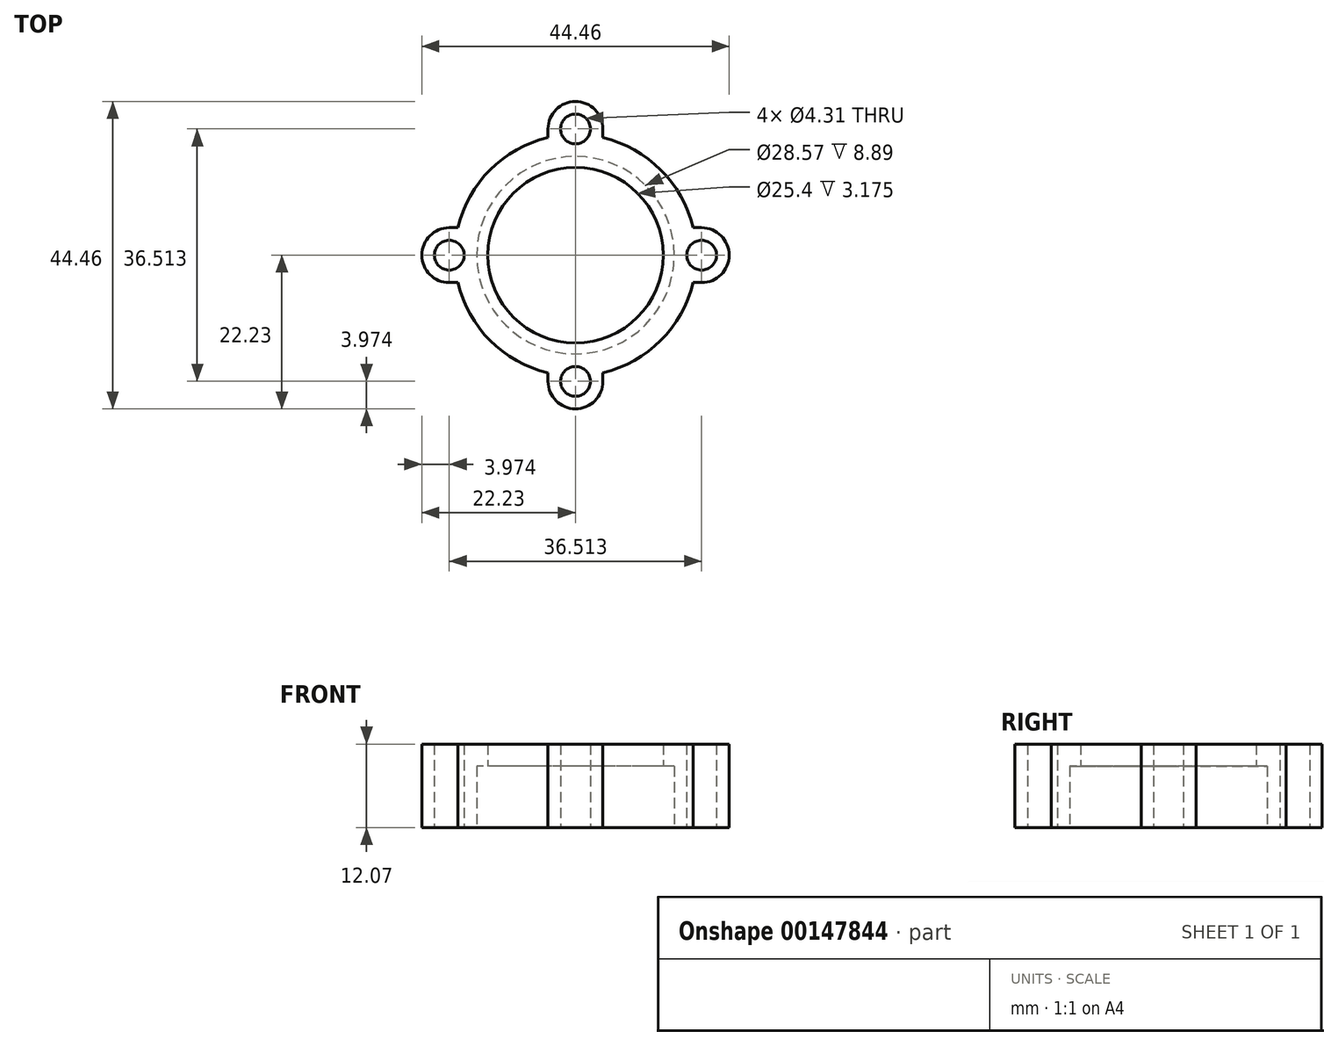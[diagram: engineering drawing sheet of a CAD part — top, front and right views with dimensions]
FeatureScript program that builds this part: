
annotation { "Feature Type Name" : "Feature", "Feature Type Description" : "" }
export const myFeature = defineFeature(function(context is Context, id is Id, definition is map)
    precondition{}
    {
        {
            var Q0;
            Q0=qCreatedBy(makeId("Top.planeOp"),FACE);
            var sketch = newSketch(context, id + "F0", { "sketchPlane" : qUnion([Q0])});
            skCircle(sketch, "E0", {"center": v(0, 0) * mm, "radius": 14.29 * mm});
            skLineSegment(sketch, "E1", {"start": v(-18.26, 0) * mm, "end": v(18.26, 0) * mm, "construction": true});
            skLineSegment(sketch, "E2", {"start": v(0, 18.26) * mm, "end": v(0, -18.26) * mm, "construction": true});
            skLineSegment(sketch, "E3.bottom", {"start": v(-3.97, 18.26) * mm, "end": v(3.97, 18.26) * mm, "construction": true});
            skLineSegment(sketch, "E3.left", {"start": v(3.97, 18.26) * mm, "end": v(3.97, 17) * mm});
            skLineSegment(sketch, "E3.right", {"start": v(-3.97, 18.26) * mm, "end": v(-3.97, 17) * mm});
            skLineSegment(sketch, "E4.bottom", {"start": v(18.26, -3.97) * mm, "end": v(17, -3.97) * mm});
            skLineSegment(sketch, "E4.top", {"start": v(18.26, 3.97) * mm, "end": v(17, 3.97) * mm});
            skLineSegment(sketch, "E4.left", {"start": v(18.26, -3.97) * mm, "end": v(18.26, 3.97) * mm, "construction": true});
            skLineSegment(sketch, "E5.bottom", {"start": v(-3.97, -18.26) * mm, "end": v(3.97, -18.26) * mm, "construction": true});
            skLineSegment(sketch, "E5.left", {"start": v(-3.97, -18.26) * mm, "end": v(-3.97, -17) * mm});
            skLineSegment(sketch, "E5.right", {"start": v(3.97, -18.26) * mm, "end": v(3.97, -17) * mm});
            skLineSegment(sketch, "E6.bottom", {"start": v(-18.26, 3.97) * mm, "end": v(-17, 3.97) * mm});
            skLineSegment(sketch, "E6.top", {"start": v(-18.26, -3.97) * mm, "end": v(-17, -3.97) * mm});
            skLineSegment(sketch, "E6.left", {"start": v(-18.26, 3.97) * mm, "end": v(-18.26, -3.97) * mm, "construction": true});
            skArc(sketch, "E7", {"start": v(17, 3.97) * mm, "mid": v(12.35, 12.35) * mm, "end": v(3.97, 17) * mm});
            skArc(sketch, "E8", {"start": v(-3.97, 17) * mm, "mid": v(-12.35, 12.35) * mm, "end": v(-17, 3.97) * mm});
            skArc(sketch, "E9", {"start": v(-17, -3.97) * mm, "mid": v(-12.35, -12.35) * mm, "end": v(-3.97, -17) * mm});
            skArc(sketch, "E10", {"start": v(3.97, -17) * mm, "mid": v(12.35, -12.35) * mm, "end": v(17, -3.97) * mm});
            skArc(sketch, "E11", {"start": v(3.97, 18.26) * mm, "mid": v(0, 22.22) * mm, "end": v(-3.97, 18.26) * mm});
            skArc(sketch, "E12", {"start": v(18.26, -3.97) * mm, "mid": v(22.22, 0) * mm, "end": v(18.26, 3.97) * mm});
            skArc(sketch, "E13", {"start": v(-3.97, -18.26) * mm, "mid": v(0, -22.22) * mm, "end": v(3.97, -18.26) * mm});
            skArc(sketch, "E14", {"start": v(-18.26, 3.97) * mm, "mid": v(-22.22, 0) * mm, "end": v(-18.26, -3.97) * mm});
            skCircle(sketch, "E15", {"center": v(0, 18.26) * mm, "radius": 2.15 * mm});
            skCircle(sketch, "E16", {"center": v(18.26, 0) * mm, "radius": 2.15 * mm});
            skCircle(sketch, "E17", {"center": v(0, -18.26) * mm, "radius": 2.15 * mm});
            skCircle(sketch, "E18", {"center": v(-18.26, 0) * mm, "radius": 2.15 * mm});
            skArc(sketch, "E19", {"start": v(-3.97, 18.26) * mm, "mid": v(0, 14.29) * mm, "end": v(3.97, 18.26) * mm, "construction": true});
            skSolve(sketch);
        }
        {
            var Q0;
            Q0=qSketchRegion(id+"F0",true);
            extrude(context, id + "F1", {"entities" : qUnion([Q0]), "depth" : 8.9 * mm});
        }
        {
            var Q0;
            Q0=makeQuery(id+"F1.opExtrude","CAP_FACE",FACE,{"disambiguationData":[OSD([sQuery(id+"F0.wireOp",EDGE,"E0"),sQuery(id+"F0.wireOp",EDGE,"E3.left"),sQuery(id+"F0.wireOp",EDGE,"E3.right"),sQuery(id+"F0.wireOp",EDGE,"E4.bottom"),sQuery(id+"F0.wireOp",EDGE,"E4.top"),sQuery(id+"F0.wireOp",EDGE,"E5.left"),sQuery(id+"F0.wireOp",EDGE,"E5.right"),sQuery(id+"F0.wireOp",EDGE,"E6.bottom"),sQuery(id+"F0.wireOp",EDGE,"E6.top"),sQuery(id+"F0.wireOp",EDGE,"E7"),sQuery(id+"F0.wireOp",EDGE,"E8"),sQuery(id+"F0.wireOp",EDGE,"E9"),sQuery(id+"F0.wireOp",EDGE,"E10"),sQuery(id+"F0.wireOp",EDGE,"E11"),sQuery(id+"F0.wireOp",EDGE,"E12"),sQuery(id+"F0.wireOp",EDGE,"E13"),sQuery(id+"F0.wireOp",EDGE,"E14"),sQuery(id+"F0.wireOp",EDGE,"E15"),sQuery(id+"F0.wireOp",EDGE,"E16"),sQuery(id+"F0.wireOp",EDGE,"E17"),sQuery(id+"F0.wireOp",EDGE,"E18")])],"isStart":false});
            var sketch = newSketch(context, id + "F2", { "sketchPlane" : qUnion([Q0])});
            skCircle(sketch, "E20", {"center": v(0, 0) * mm, "radius": 12.7 * mm});
            skSolve(sketch);
        }
        {
            var Q0;
            Q0=makeQuery(id+"F2.imprint","IMPRINT",FACE,{"disambiguationData":[TD([[makeQuery(id+"F2.imprint","IMPRINT",EDGE,{"derivedFrom":sQuery(id+"F2.wireOp",EDGE,"E20")}),-1.0]])]});
            var Q1;
            Q1=makeQuery(id+"F2.imprint","IMPRINT",FACE,{"disambiguationData":[TD([[makeQuery(id+"F2.imprint","IMPRINT",EDGE,{"derivedFrom":makeQuery(id+"F1.opExtrude","CAP_EDGE",EDGE,{"disambiguationData":[OSD([sQuery(id+"F0.wireOp",EDGE,"E0")])],"isStart":false})}),-1.0]])]});
            extrude(context, id + "F3", {"entities" : qUnion([Q0, Q1]), "operationType" : NewBodyOperationType.ADD, "depth" : 3.17 * mm});
        }
    });
